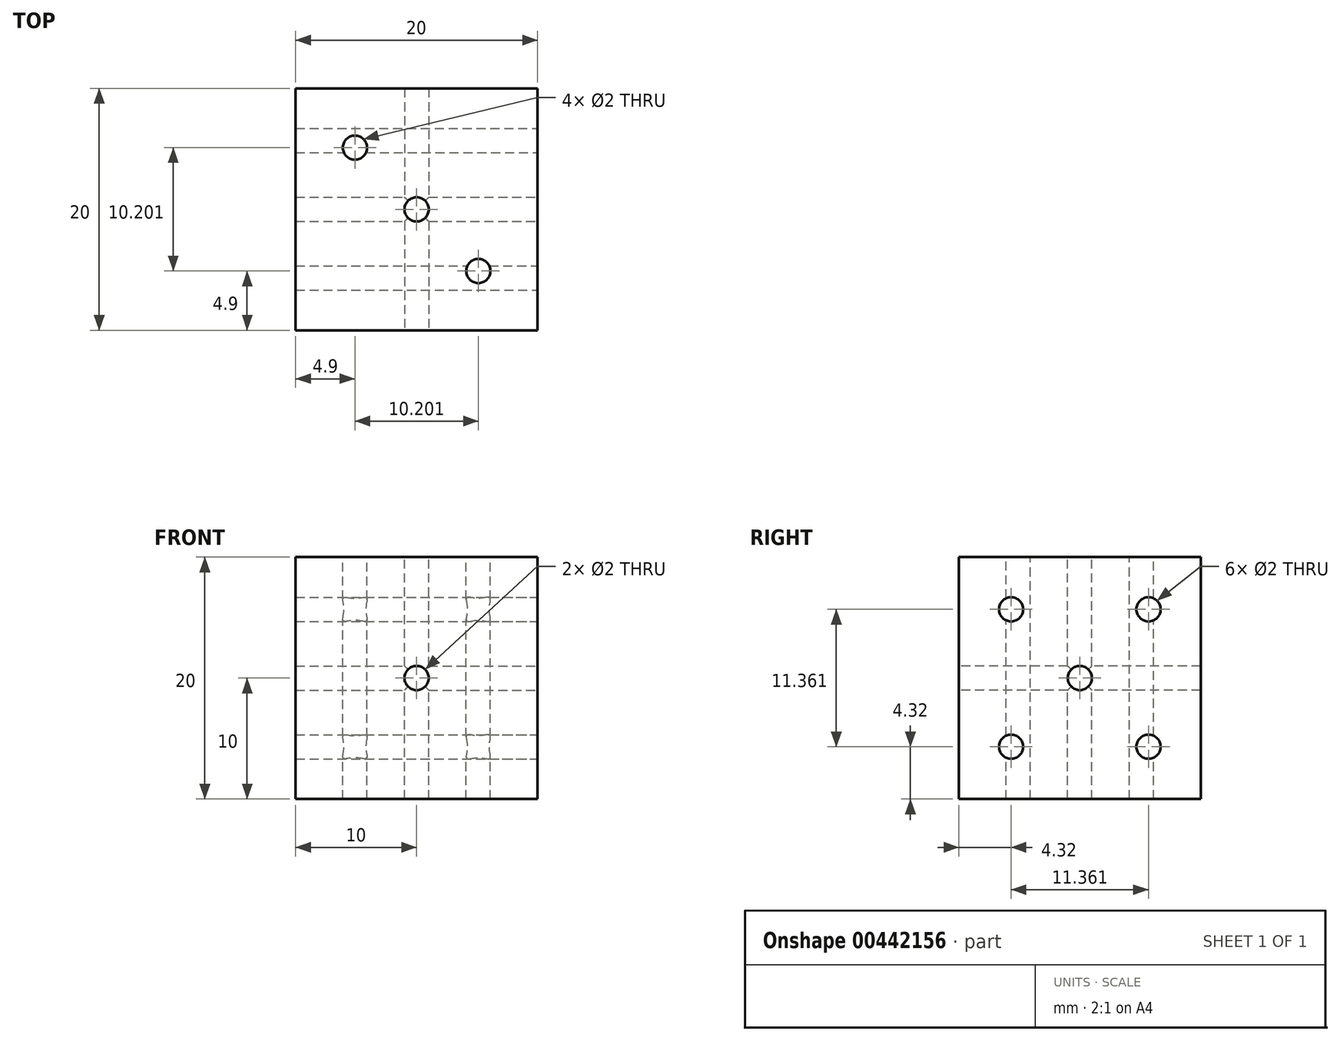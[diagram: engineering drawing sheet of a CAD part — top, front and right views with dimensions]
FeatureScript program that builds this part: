
annotation { "Feature Type Name" : "Feature", "Feature Type Description" : "" }
export const myFeature = defineFeature(function(context is Context, id is Id, definition is map)
    precondition{}
    {
        {
            var Q0;
            Q0=qCreatedBy(makeId("Front.planeOp"),FACE);
            var sketch = newSketch(context, id + "F0", { "sketchPlane" : qUnion([Q0])});
            skLineSegment(sketch, "E0.bottom", {"start": v(0, 0) * mm, "end": v(20, 0) * mm});
            skLineSegment(sketch, "E0.top", {"start": v(0, 20) * mm, "end": v(20, 20) * mm});
            skLineSegment(sketch, "E0.left", {"start": v(0, 0) * mm, "end": v(0, 20) * mm});
            skLineSegment(sketch, "E0.right", {"start": v(20, 0) * mm, "end": v(20, 20) * mm});
            skSolve(sketch);
        }
        {
            var Q0;
            Q0 = qSketchRegion(id + "F0", true);
            extrude(context, id + "F1", {"entities" : qUnion([Q0]), "depth" : 20 * mm});
        }
        {
            var Q0;
            Q0=makeQuery(id+"F1.opExtrude","CAP_FACE",FACE,{"disambiguationData":[OSD([sQuery(id+"F0.wireOp",EDGE,"E0.bottom"),sQuery(id+"F0.wireOp",EDGE,"E0.top"),sQuery(id+"F0.wireOp",EDGE,"E0.left"),sQuery(id+"F0.wireOp",EDGE,"E0.right")])],"isStart":false});
            var sketch = newSketch(context, id + "F2", { "sketchPlane" : qUnion([Q0])});
            skLineSegment(sketch, "E1", {"start": v(0, 0) * mm, "end": v(20, 20) * mm});
            skLineSegment(sketch, "E2", {"start": v(0, 20) * mm, "end": v(20, 0) * mm});
            skCircle(sketch, "E3", {"center": v(10, 10) * mm, "radius": 2.94 * mm});
            skSolve(sketch);
        }
        {
            var Q0;
            Q0=sQuery(id+"F2.wireOp",VERTEX,"E3.center");
            var Q1;
            Q1=makeQuery(id+"F1.opExtrude","SWEPT_BODY",BODY,{"disambiguationData":[OSD([sQuery(id+"F0.wireOp",EDGE,"E0.bottom"),sQuery(id+"F0.wireOp",EDGE,"E0.top"),sQuery(id+"F0.wireOp",EDGE,"E0.left"),sQuery(id+"F0.wireOp",EDGE,"E0.right")])]});
            hole(context, id + "F3", {"style" : HoleStyle.SIMPLE, "endStyle" : HoleEndStyle.THROUGH, "holeDiameter" : 2 * mm, "isTappedThrough" : true, "tappedDepth" : 12 * mm, "tapClearance" : 3, "locations" : qUnion([Q0]), "scope" : qUnion([Q1])});
        }
        {
            var Q0;
            Q0=makeQuery(id+"F1.opExtrude","SWEPT_FACE",FACE,{"disambiguationData":[OSD([sQuery(id+"F0.wireOp",EDGE,"E0.top")])]});
            var sketch = newSketch(context, id + "F4", { "sketchPlane" : qUnion([Q0])});
            skLineSegment(sketch, "E4", {"start": v(0, 0) * mm, "end": v(20, -20) * mm});
            skLineSegment(sketch, "E5", {"start": v(0, -20) * mm, "end": v(20, 0) * mm});
            skCircle(sketch, "E6", {"center": v(10, -10) * mm, "radius": 7.21 * mm});
            skCircle(sketch, "E7", {"center": v(4.9, -4.9) * mm, "radius": 2.38 * mm});
            skCircle(sketch, "E8", {"center": v(15.1, -15.1) * mm, "radius": 2.2 * mm});
            skSolve(sketch);
        }
        {
            var Q0;
            Q0=sQuery(id+"F4.wireOp",VERTEX,"E7.center");
            var Q1;
            Q1=sQuery(id+"F4.wireOp",VERTEX,"E6.center");
            var Q2;
            Q2=sQuery(id+"F4.wireOp",VERTEX,"E8.center");
            var Q3;
            Q3=makeQuery(id+"F1.opExtrude","SWEPT_BODY",BODY,{"disambiguationData":[OSD([sQuery(id+"F0.wireOp",EDGE,"E0.bottom"),sQuery(id+"F0.wireOp",EDGE,"E0.top"),sQuery(id+"F0.wireOp",EDGE,"E0.left"),sQuery(id+"F0.wireOp",EDGE,"E0.right")])]});
            hole(context, id + "F5", {"style" : HoleStyle.SIMPLE, "endStyle" : HoleEndStyle.THROUGH, "holeDiameter" : 2 * mm, "isTappedThrough" : true, "tappedDepth" : 12 * mm, "tapClearance" : 3, "locations" : qUnion([Q0, Q1, Q2]), "scope" : qUnion([Q3])});
        }
        {
            var Q0;
            Q0=makeQuery(id+"F1.opExtrude","SWEPT_FACE",FACE,{"disambiguationData":[OSD([sQuery(id+"F0.wireOp",EDGE,"E0.right")])]});
            var sketch = newSketch(context, id + "F6", { "sketchPlane" : qUnion([Q0])});
            skLineSegment(sketch, "E9", {"start": v(-20, 20) * mm, "end": v(0, 0) * mm});
            skLineSegment(sketch, "E10", {"start": v(0, 20) * mm, "end": v(-20, 0) * mm});
            skCircle(sketch, "E11", {"center": v(-10, 10) * mm, "radius": 8.03 * mm});
            skCircle(sketch, "E12", {"center": v(-15.68, 15.68) * mm, "radius": 1.54 * mm});
            skCircle(sketch, "E13", {"center": v(-4.32, 15.68) * mm, "radius": 1.8 * mm});
            skCircle(sketch, "E14", {"center": v(-10, 10) * mm, "radius": 1.8 * mm});
            skCircle(sketch, "E15", {"center": v(-15.68, 4.32) * mm, "radius": 1.73 * mm});
            skCircle(sketch, "E16", {"center": v(-4.32, 4.32) * mm, "radius": 1.54 * mm});
            skSolve(sketch);
        }
        {
            var Q0;
            Q0=sQuery(id+"F6.wireOp",VERTEX,"E14.center");
            var Q1;
            Q1=sQuery(id+"F6.wireOp",VERTEX,"E12.center");
            var Q2;
            Q2=sQuery(id+"F6.wireOp",VERTEX,"E15.center");
            var Q3;
            Q3=sQuery(id+"F6.wireOp",VERTEX,"E16.center");
            var Q4;
            Q4=sQuery(id+"F6.wireOp",VERTEX,"E13.center");
            var Q5;
            Q5=makeQuery(id+"F1.opExtrude","SWEPT_BODY",BODY,{"disambiguationData":[OSD([sQuery(id+"F0.wireOp",EDGE,"E0.bottom"),sQuery(id+"F0.wireOp",EDGE,"E0.top"),sQuery(id+"F0.wireOp",EDGE,"E0.left"),sQuery(id+"F0.wireOp",EDGE,"E0.right")])]});
            hole(context, id + "F7", {"style" : HoleStyle.SIMPLE, "endStyle" : HoleEndStyle.THROUGH, "holeDiameter" : 2 * mm, "isTappedThrough" : true, "tappedDepth" : 12 * mm, "tapClearance" : 3, "locations" : qUnion([Q0, Q1, Q2, Q3, Q4]), "scope" : qUnion([Q5])});
        }
    });
